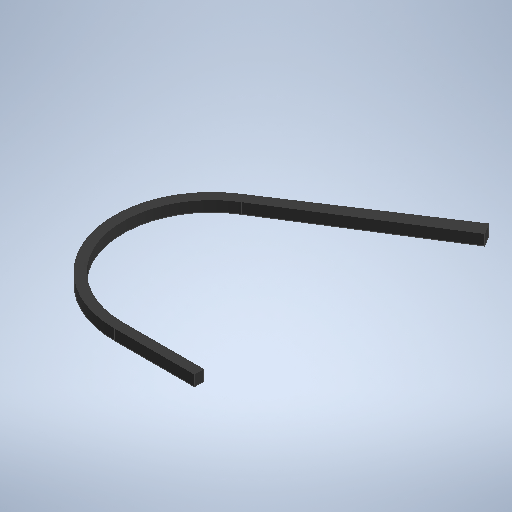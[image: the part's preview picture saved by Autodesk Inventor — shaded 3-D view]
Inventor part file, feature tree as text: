
AUTODESK INVENTOR PART (.ipt)
format: ipt  version: 2025.2 (Build 292293000, 293)  size: 257,536 bytes
history: native  units: mm
features: other x1, extrude x1, sketch x1
ambient origin geometry x8: Origin, YZ Plane, XZ Plane, XY Plane, X Axis, Y Axis, Z Axis, Center Point
bodies: Body1 (feature_tree)
feature tree (3):
  other  "ソリッド1"
  extrude  "押し出し1"  Depth=5.0mm TaperAngle=0.0deg
  sketch  "スケッチ1"
